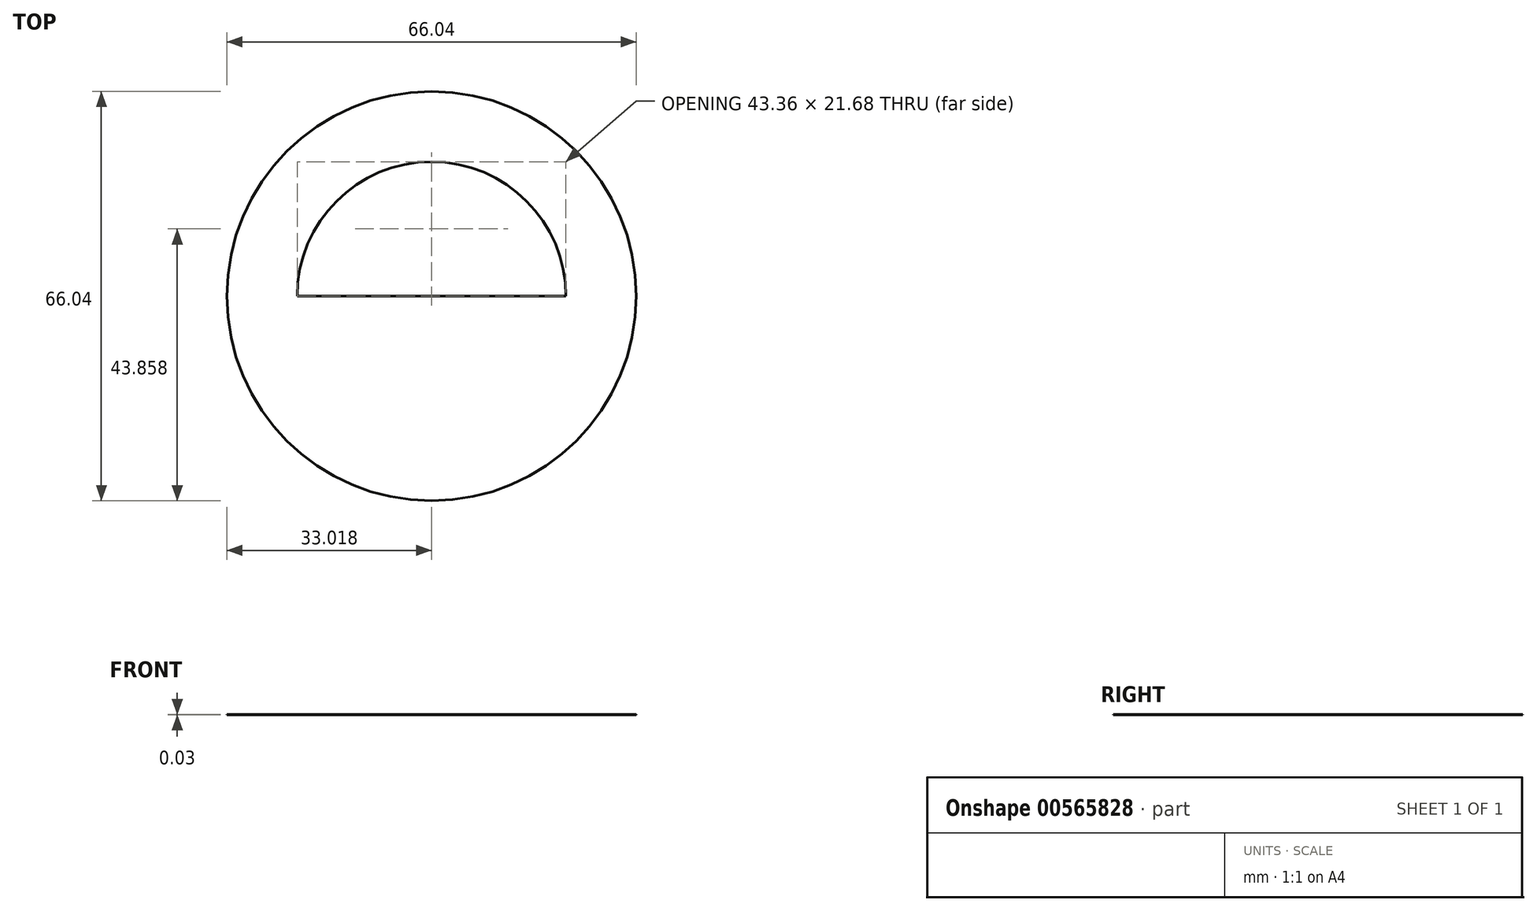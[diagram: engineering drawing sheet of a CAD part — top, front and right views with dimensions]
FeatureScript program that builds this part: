
annotation { "Feature Type Name" : "Feature", "Feature Type Description" : "" }
export const myFeature = defineFeature(function(context is Context, id is Id, definition is map)
    precondition{}
    {
        {
            var Q0;
            Q0=qCreatedBy(makeId("Top.planeOp"),FACE);
            var sketch = newSketch(context, id + "F0", { "sketchPlane" : qUnion([Q0])});
            skLineSegment(sketch, "E0", {"start": v(-246.83, -15.76) * mm, "end": v(-203.47, -15.76) * mm});
            skCircle(sketch, "E1", {"center": v(-225.15, -15.76) * mm, "radius": 33.02 * mm});
            skArc(sketch, "E2", {"start": v(-246.83, -15.76) * mm, "mid": v(-225.15, 5.92) * mm, "end": v(-203.47, -15.76) * mm});
            skSolve(sketch);
        }
        {
            var Q0;
            Q0=makeQuery(id+"F0.imprint","IMPRINT",FACE,{"disambiguationData":[TD([[makeQuery(id+"F0.imprint","IMPRINT",EDGE,{"derivedFrom":sQuery(id+"F0.wireOp",EDGE,"E0")}),-1.0]])]});
            extrude(context, id + "F1", {"entities" : qUnion([Q0]), "depth" : 0.03 * mm, "offsetDistance" : 25.4 * mm});
        }
    });
